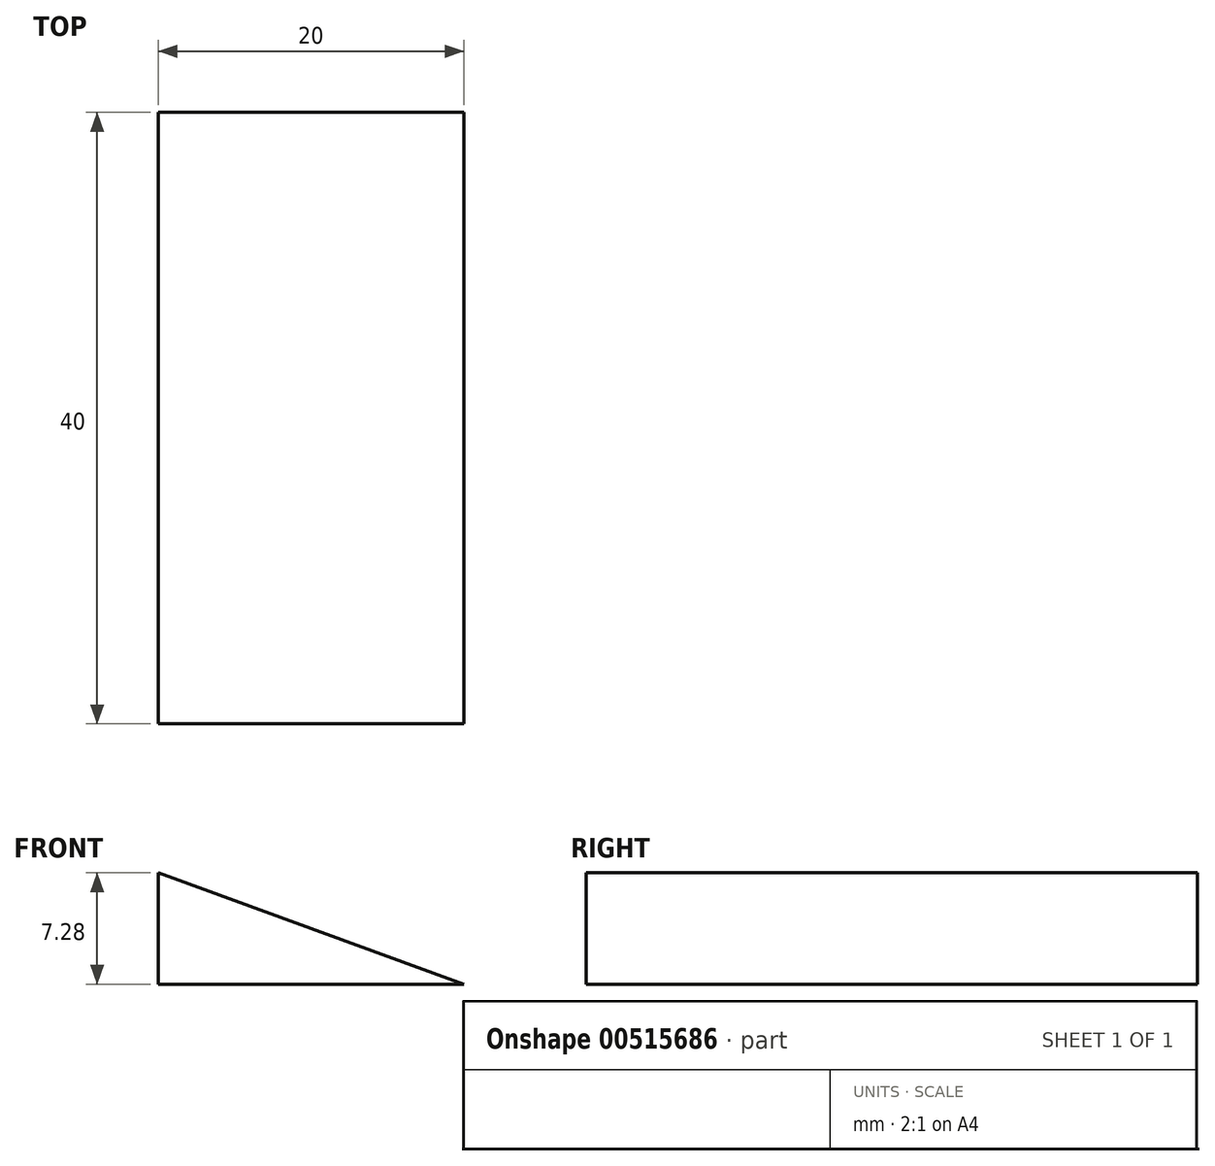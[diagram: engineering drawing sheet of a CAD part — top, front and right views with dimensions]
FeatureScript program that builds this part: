
annotation { "Feature Type Name" : "Feature", "Feature Type Description" : "" }
export const myFeature = defineFeature(function(context is Context, id is Id, definition is map)
    precondition{}
    {
        {
            var Q0;
            Q0=qCreatedBy(makeId("Front.planeOp"),FACE);
            var sketch = newSketch(context, id + "F0", { "sketchPlane" : qUnion([Q0])});
            skLineSegment(sketch, "E0", {"start": v(-5.91, 4.63) * mm, "end": v(-5.91, -2.65) * mm});
            skLineSegment(sketch, "E1", {"start": v(-5.91, -2.65) * mm, "end": v(14.09, -2.65) * mm});
            skLineSegment(sketch, "E2", {"start": v(14.09, -2.65) * mm, "end": v(-5.91, 4.63) * mm});
            skSolve(sketch);
        }
        {
            var Q0;
            Q0 = qSketchRegion(id + "F0", true);
            extrude(context, id + "F1", {"entities" : qUnion([Q0]), "depth" : 40 * mm, "offsetDistance" : 25 * mm});
        }
    });
